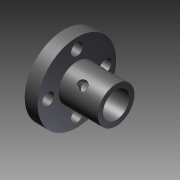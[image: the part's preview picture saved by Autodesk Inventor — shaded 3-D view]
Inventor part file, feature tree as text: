
AUTODESK INVENTOR PART (.ipt)
format: ipt  version: 2011 SP1 (Build 150282100, 282)  size: 148,992 bytes
history: native  units: mm
features: other x14, sketch x7, hole x4, revolve x3, thread x2
ambient origin geometry x8: Origin, YZ Plane, XZ Plane, XY Plane, X Axis, Y Axis, Z Axis, Center Point
bodies: Solid1 (feature_tree)
feature tree (30):
  revolve  "Revolution1"  Angle=360.0deg
  revolve  "Revolution2"  Angle=360.0deg
  thread  "Thread1"  [1 undecoded]
  hole  "Hole1"  [1 undecoded]
  hole  "Hole2"  [1 undecoded]
  hole  "Hole3"  [1 undecoded]
  hole  "Hole4"  [1 undecoded]
  revolve  "Revolution3"  [1 undecoded]
  thread  "Thread2"  [1 undecoded]
  other  "to_screw1_XY"
  other  "to_screw1_YZ"
  other  "to_screw1_ZX"
  other  "to_screw1_X"
  other  "to_screw1_Y"
  other  "to_screw1_Z"
  other  "to_screw1_Center"
  other  "to_screw2_XY"
  other  "to_screw2_YZ"
  other  "to_screw2_ZX"
  other  "to_screw2_X"
  other  "to_screw2_Y"
  other  "to_screw2_Z"
  other  "to_screw2_Center"
  sketch  "Sketch_1"  dims[d0=360.0deg d1=360.0deg]
  sketch  "Sketch_3"  dims[d4=4.5mm d5=6.0mm d6=4.0mm d7=2.0mm d8=90.0deg d9=5.0mm d10=0.0mm]
  sketch  "Sketch3"  dims[d11=4.5mm d12=6.0mm d13=4.0mm d14=2.0mm d15=90.0deg d16=5.0mm d17=0.0mm]
  sketch  "Sketch4"  dims[d18=4.5mm d19=6.0mm d20=4.0mm d21=2.0mm d22=90.0deg d23=5.0mm d24=0.0mm]
  sketch  "Sketch5"  dims[d25=4.5mm d26=6.0mm d27=4.0mm d28=2.0mm d29=90.0deg d30=5.0mm d31=0.0mm d32=360.0deg d33=2.121mm d34=0.0mm]
  sketch  "Sketch6"
  sketch  "Sketch_2"  dims[d2=2.121mm d3=0.0mm]
note: 7 required parameter values undecoded (feature->parameter linkage not recoverable at this tier; creation-order binding heuristic only, values carry confidence <= 0.55)
